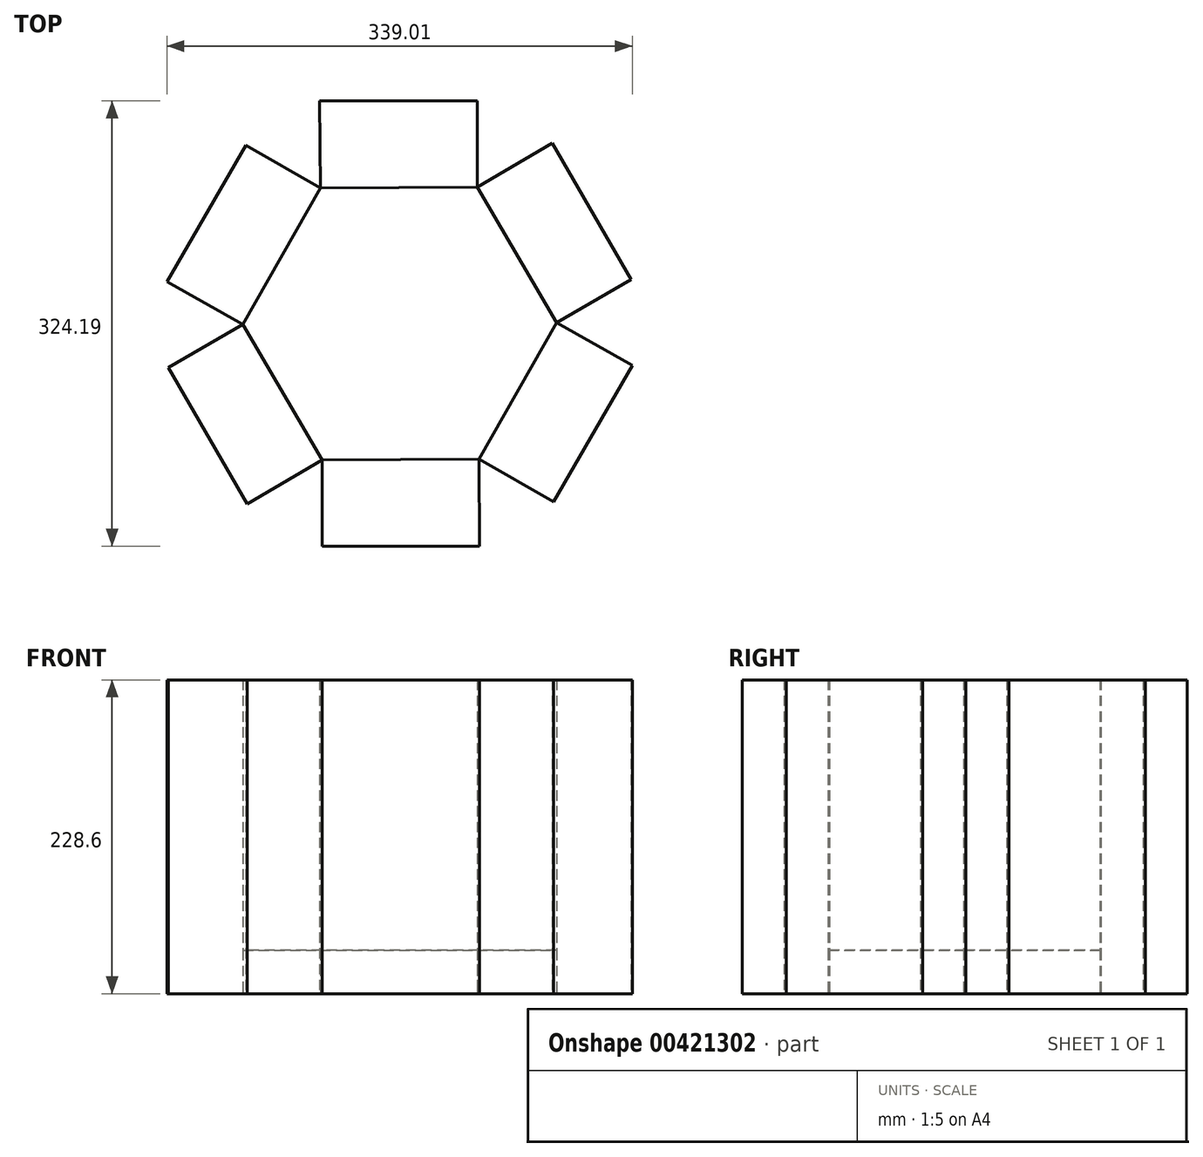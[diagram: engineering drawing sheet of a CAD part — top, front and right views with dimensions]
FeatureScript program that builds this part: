
annotation { "Feature Type Name" : "Feature", "Feature Type Description" : "" }
export const myFeature = defineFeature(function(context is Context, id is Id, definition is map)
    precondition{}
    {
        {
            var Q0;
            Q0=qCreatedBy(makeId("Top.planeOp"),FACE);
            var sketch = newSketch(context, id + "F0", { "sketchPlane" : qUnion([Q0])});
            skCircle(sketch, "E0.cCircle", {"center": v(0.68, -0.68) * mm, "radius": 98.99 * mm, "construction": true});
            skLineSegment(sketch, "E0.0", {"start": v(-57.15, 97.92) * mm, "end": v(57.15, 98.7) * mm});
            skLineSegment(sketch, "E0.1", {"start": v(57.15, 98.7) * mm, "end": v(114.97, 0.1) * mm});
            skLineSegment(sketch, "E0.2", {"start": v(114.97, 0.1) * mm, "end": v(58.5, -99.27) * mm});
            skLineSegment(sketch, "E0.3", {"start": v(58.5, -99.27) * mm, "end": v(-55.8, -100.05) * mm});
            skLineSegment(sketch, "E0.4", {"start": v(-55.8, -100.05) * mm, "end": v(-113.62, -1.46) * mm});
            skLineSegment(sketch, "E0.5", {"start": v(-113.62, -1.46) * mm, "end": v(-57.15, 97.92) * mm});
            skPoint(sketch, "E0.0.midPoint", {"position": v(0, 98.3) * mm});
            skLineSegment(sketch, "E1", {"start": v(-57.15, 97.92) * mm, "end": v(-57.58, 161.42) * mm});
            skLineSegment(sketch, "E2.bottom", {"start": v(-57.58, 161.42) * mm, "end": v(57.15, 161.42) * mm});
            skLineSegment(sketch, "E2.right", {"start": v(57.15, 161.42) * mm, "end": v(57.15, 98.7) * mm});
            skSolve(sketch);
        }
        {
            var Q0;
            Q0=makeQuery(id+"F0.imprint","IMPRINT",FACE,{"disambiguationData":[TD([[makeQuery(id+"F0.imprint","IMPRINT",EDGE,{"derivedFrom":sQuery(id+"F0.wireOp",EDGE,"E0.0")}),-1.0]])]});
            extrude(context, id + "F1", {"entities" : qUnion([Q0]), "depth" : 31.75 * mm});
        }
        {
            var Q0;
            Q0=makeQuery(id+"F0.imprint","IMPRINT",FACE,{"disambiguationData":[TD([[makeQuery(id+"F0.imprint","IMPRINT",EDGE,{"derivedFrom":sQuery(id+"F0.wireOp",EDGE,"E0.0")}),1.0]])]});
            extrude(context, id + "F2", {"entities" : qUnion([Q0]), "operationType" : NewBodyOperationType.ADD, "depth" : 228.6 * mm});
        }
        {
            var Q0;
            Q0=makeQuery(id+"F1.opExtrude","SWEPT_BODY",BODY,{"disambiguationData":[OSD([sQuery(id+"F0.wireOp",EDGE,"E0.0"),sQuery(id+"F0.wireOp",EDGE,"E0.1"),sQuery(id+"F0.wireOp",EDGE,"E0.2"),sQuery(id+"F0.wireOp",EDGE,"E0.3"),sQuery(id+"F0.wireOp",EDGE,"E0.4"),sQuery(id+"F0.wireOp",EDGE,"E0.5")])]});
            var Q1;
            Q1=sQuery(id+"F0.wireOp",EDGE,"E0.cCircle");
            circularPattern(context, id + "F3", {"entities" : qUnion([Q0]), "axis" : qUnion([Q1]), "angle" : 360 * degree, "instanceCount" : 6, "equalSpace" : true});
        }
    });
